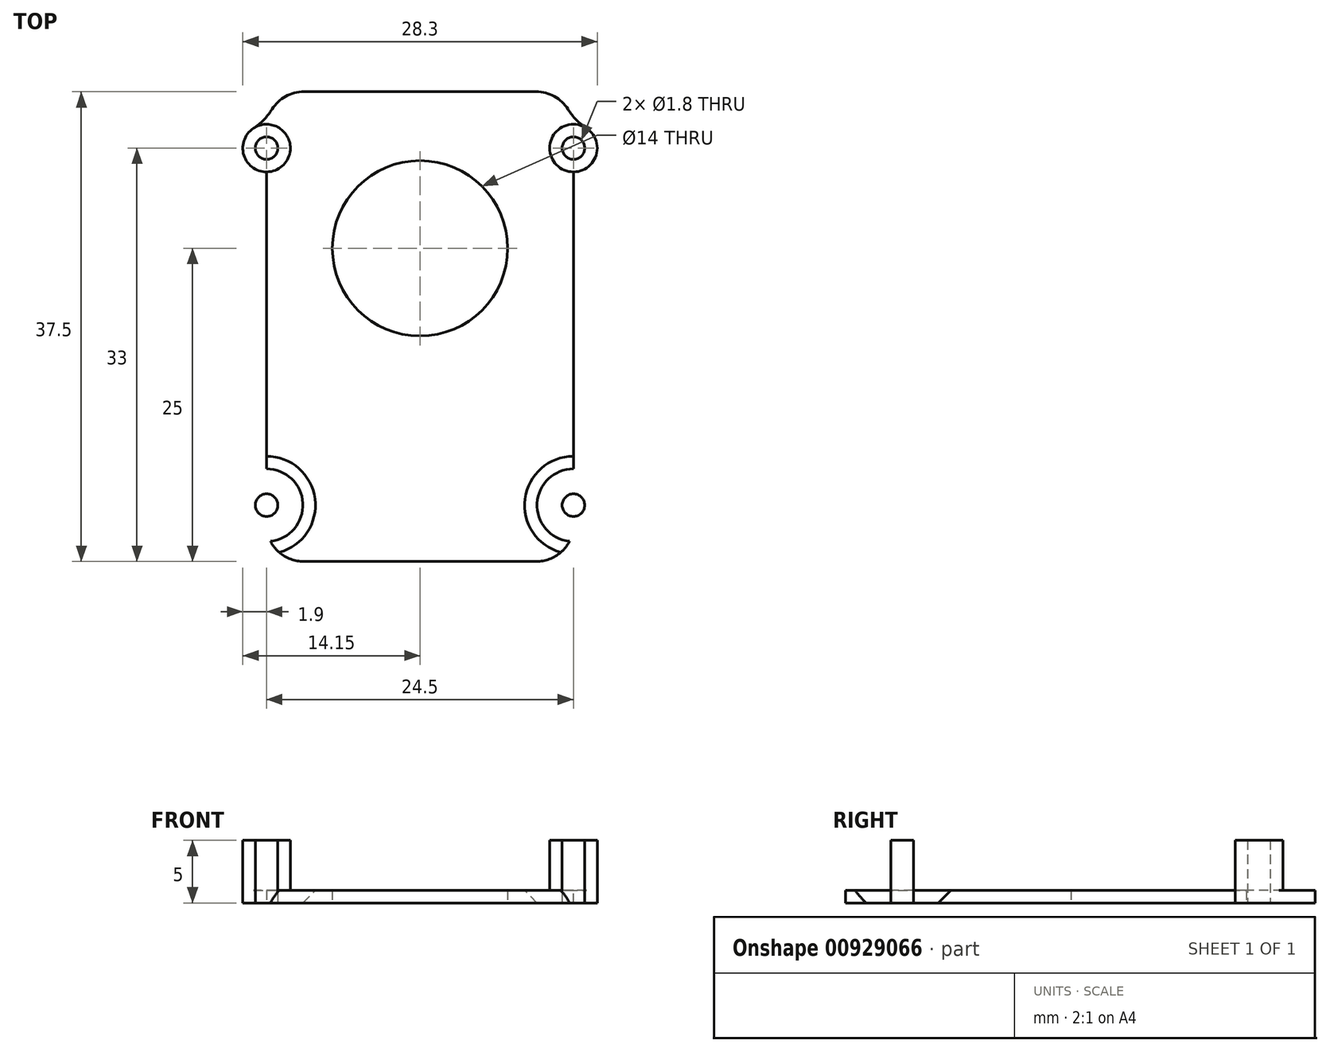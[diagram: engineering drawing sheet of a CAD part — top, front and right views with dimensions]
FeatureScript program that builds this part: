
annotation { "Feature Type Name" : "Feature", "Feature Type Description" : "" }
export const myFeature = defineFeature(function(context is Context, id is Id, definition is map)
    precondition{}
    {
        {
            var Q0;
            Q0=qCreatedBy(makeId("Top.planeOp"),FACE);
            var sketch = newSketch(context, id + "F0", { "sketchPlane" : qUnion([Q0])});
            skCircle(sketch, "E0", {"center": v(-12.25, 14.25) * mm, "radius": 0.9 * mm});
            skLineSegment(sketch, "E1", {"start": v(-12.25, 14.25) * mm, "end": v(12.25, 14.25) * mm, "construction": true});
            skCircle(sketch, "E2", {"center": v(12.25, 14.25) * mm, "radius": 0.9 * mm});
            skLineSegment(sketch, "E3", {"start": v(12.25, 0) * mm, "end": v(-12.25, 0) * mm, "construction": true});
            skLineSegment(sketch, "E4", {"start": v(0, 0) * mm, "end": v(0, 23) * mm, "construction": true});
            skCircle(sketch, "E5.0", {"center": v(-12.25, 14.25) * mm, "radius": 1.9 * mm});
            skCircle(sketch, "E6.0", {"center": v(12.25, 14.25) * mm, "radius": 1.9 * mm});
            skCircle(sketch, "E7.MirrorC", {"center": v(-12.25, -14.25) * mm, "radius": 1.9 * mm});
            skCircle(sketch, "E8.MirrorC", {"center": v(-12.25, -14.25) * mm, "radius": 0.9 * mm});
            skCircle(sketch, "E9.MirrorC", {"center": v(12.25, -14.25) * mm, "radius": 1.9 * mm});
            skCircle(sketch, "E10.MirrorC", {"center": v(12.25, -14.25) * mm, "radius": 0.9 * mm});
            skLineSegment(sketch, "E11", {"start": v(-12.25, -12.35) * mm, "end": v(-12.25, 12.35) * mm});
            skLineSegment(sketch, "E12", {"start": v(12.25, 12.35) * mm, "end": v(12.25, -12.35) * mm});
            skLineSegment(sketch, "E13", {"start": v(-12.25, 18.75) * mm, "end": v(12.25, 18.75) * mm});
            skLineSegment(sketch, "E14", {"start": v(-12.25, 18.75) * mm, "end": v(-12.25, 16.15) * mm});
            skLineSegment(sketch, "E15", {"start": v(12.25, 18.75) * mm, "end": v(12.25, 16.15) * mm});
            skLineSegment(sketch, "E16.MirrorCS", {"start": v(-12.25, -18.75) * mm, "end": v(-12.25, -16.15) * mm});
            skLineSegment(sketch, "E17.MirrorCS", {"start": v(-12.25, -18.75) * mm, "end": v(12.25, -18.75) * mm});
            skLineSegment(sketch, "E18.MirrorCS", {"start": v(12.25, -18.75) * mm, "end": v(12.25, -16.15) * mm});
            skCircle(sketch, "E19", {"center": v(0, 6.25) * mm, "radius": 7 * mm});
            skSolve(sketch);
        }
        {
            var Q0;
            {var subQ3=sQuery(id+"F0.wireOp",EDGE,"E11");Q0=makeQuery(id+"F0.imprint","IMPRINT",FACE,{"disambiguationData":[TD([[makeQuery(id+"F0.imprint","IMPRINT",EDGE,{"derivedFrom":subQ3}),-1.0]])]});}
            extrude(context, id + "F1", {"entities" : qUnion([Q0]), "depth" : 1 * mm, "offsetDistance" : 25 * mm});
        }
        {
            var Q0;
            Q0=makeQuery(id+"F0.imprint","IMPRINT",FACE,{"disambiguationData":[TD([[makeQuery(id+"F0.imprint","IMPRINT",EDGE,{"derivedFrom":sQuery(id+"F0.wireOp",EDGE,"E0")}),-1.0]])]});
            var Q1;
            Q1=makeQuery(id+"F0.imprint","IMPRINT",FACE,{"disambiguationData":[TD([[makeQuery(id+"F0.imprint","IMPRINT",EDGE,{"derivedFrom":sQuery(id+"F0.wireOp",EDGE,"E2")}),-1.0]])]});
            var Q2;
            Q2=makeQuery(id+"F0.imprint","IMPRINT",FACE,{"disambiguationData":[TD([[makeQuery(id+"F0.imprint","IMPRINT",EDGE,{"derivedFrom":sQuery(id+"F0.wireOp",EDGE,"E10.MirrorC")}),1.0]])]});
            var Q3;
            Q3=makeQuery(id+"F0.imprint","IMPRINT",FACE,{"disambiguationData":[TD([[makeQuery(id+"F0.imprint","IMPRINT",EDGE,{"derivedFrom":sQuery(id+"F0.wireOp",EDGE,"E8.MirrorC")}),1.0]])]});
            extrude(context, id + "F2", {"entities" : qUnion([Q0, Q1, Q2, Q3]), "operationType" : NewBodyOperationType.ADD, "depth" : 5 * mm, "offsetDistance" : 25 * mm});
        }
        {
            var Q0;
            Q0=makeQuery(id+"F1.opExtrude","SWEPT_EDGE",EDGE,{"disambiguationData":[OSD([sQuery(id+"F0.wireOp",EDGE,"E16.MirrorCS"),sQuery(id+"F0.wireOp",EDGE,"E17.MirrorCS")])]});
            var Q1;
            Q1=makeQuery(id+"F1.opExtrude","SWEPT_EDGE",EDGE,{"disambiguationData":[OSD([sQuery(id+"F0.wireOp",EDGE,"E17.MirrorCS"),sQuery(id+"F0.wireOp",EDGE,"E18.MirrorCS")])]});
            var Q2;
            Q2=makeQuery(id+"F1.opExtrude","SWEPT_EDGE",EDGE,{"disambiguationData":[OSD([sQuery(id+"F0.wireOp",EDGE,"E13"),sQuery(id+"F0.wireOp",EDGE,"E15")])]});
            var Q3;
            Q3=makeQuery(id+"F1.opExtrude","SWEPT_EDGE",EDGE,{"disambiguationData":[OSD([sQuery(id+"F0.wireOp",EDGE,"E13"),sQuery(id+"F0.wireOp",EDGE,"E14")])]});
            fillet(context, id + "F3", {"entities" : qUnion([Q0, Q1, Q2, Q3]), "radius" : 3 * mm, "tangentPropagation" : true, "allowEdgeOverflow" : false});
        }
        {
            var Q0;
            Q0=makeQuery(id+"F1.opExtrude","CAP_EDGE",EDGE,{"disambiguationData":[OSD([sQuery(id+"F0.wireOp",EDGE,"E5.0")])],"isStart":false});
            var Q1;
            Q1=makeQuery(id+"F1.opExtrude","CAP_EDGE",EDGE,{"disambiguationData":[OSD([sQuery(id+"F0.wireOp",EDGE,"E7.MirrorC")])],"isStart":false});
            var Q2;
            Q2=makeQuery(id+"F1.opExtrude","CAP_EDGE",EDGE,{"disambiguationData":[OSD([sQuery(id+"F0.wireOp",EDGE,"E9.MirrorC")])],"isStart":false});
            var Q3;
            Q3=makeQuery(id+"F1.opExtrude","CAP_EDGE",EDGE,{"disambiguationData":[OSD([sQuery(id+"F0.wireOp",EDGE,"E6.0")])],"isStart":false});
            chamfer(context, id + "F4", {"entities" : qUnion([Q0, Q1, Q2, Q3]), "width" : 2 * mm, "tangentPropagation" : true});
        }
        {
            var Q0;
            Q0=makeQuery(id+"F3.opFillet","BLEND_EDGE",EDGE,{"blendedFrom":[makeQuery(id+"F1.opExtrude","SWEPT_EDGE",EDGE,{"disambiguationData":[OSD([sQuery(id+"F0.wireOp",EDGE,"E17.MirrorCS"),sQuery(id+"F0.wireOp",EDGE,"E18.MirrorCS")])]}),makeQuery(id+"F2.opExtrude","SWEPT_FACE",FACE,{"disambiguationData":[OSD([sQuery(id+"F0.wireOp",EDGE,"E9.MirrorC")])]})],"blendedInto":[makeQuery(id+"F2.opExtrude","SWEPT_FACE",FACE,{"disambiguationData":[OSD([sQuery(id+"F0.wireOp",EDGE,"E9.MirrorC")])]})]});
            var Q1;
            Q1=makeQuery(id+"F1.opExtrude","SWEPT_EDGE",EDGE,{"disambiguationData":[OSD([sQuery(id+"F0.wireOp",EDGE,"E9.MirrorC"),sQuery(id+"F0.wireOp",EDGE,"E12")])]});
            var Q2;
            Q2=makeQuery(id+"F1.opExtrude","SWEPT_EDGE",EDGE,{"disambiguationData":[OSD([sQuery(id+"F0.wireOp",EDGE,"E7.MirrorC"),sQuery(id+"F0.wireOp",EDGE,"E11")])]});
            var Q3;
            Q3=makeQuery(id+"F3.opFillet","BLEND_EDGE",EDGE,{"blendedFrom":[makeQuery(id+"F1.opExtrude","SWEPT_EDGE",EDGE,{"disambiguationData":[OSD([sQuery(id+"F0.wireOp",EDGE,"E16.MirrorCS"),sQuery(id+"F0.wireOp",EDGE,"E17.MirrorCS")])]}),makeQuery(id+"F2.opExtrude","SWEPT_FACE",FACE,{"disambiguationData":[OSD([sQuery(id+"F0.wireOp",EDGE,"E7.MirrorC")])]})],"blendedInto":[makeQuery(id+"F2.opExtrude","SWEPT_FACE",FACE,{"disambiguationData":[OSD([sQuery(id+"F0.wireOp",EDGE,"E7.MirrorC")])]})]});
            var Q4;
            Q4=makeQuery(id+"F1.opExtrude","SWEPT_EDGE",EDGE,{"disambiguationData":[OSD([sQuery(id+"F0.wireOp",EDGE,"E5.0"),sQuery(id+"F0.wireOp",EDGE,"E11")])]});
            var Q5;
            Q5=makeQuery(id+"F3.opFillet","BLEND_EDGE",EDGE,{"blendedFrom":[makeQuery(id+"F1.opExtrude","SWEPT_EDGE",EDGE,{"disambiguationData":[OSD([sQuery(id+"F0.wireOp",EDGE,"E13"),sQuery(id+"F0.wireOp",EDGE,"E14")])]}),makeQuery(id+"F2.opExtrude","SWEPT_FACE",FACE,{"disambiguationData":[OSD([sQuery(id+"F0.wireOp",EDGE,"E5.0")])]})],"blendedInto":[makeQuery(id+"F2.opExtrude","SWEPT_FACE",FACE,{"disambiguationData":[OSD([sQuery(id+"F0.wireOp",EDGE,"E5.0")])]})]});
            var Q6;
            Q6=makeQuery(id+"F3.opFillet","BLEND_EDGE",EDGE,{"blendedFrom":[makeQuery(id+"F1.opExtrude","SWEPT_EDGE",EDGE,{"disambiguationData":[OSD([sQuery(id+"F0.wireOp",EDGE,"E13"),sQuery(id+"F0.wireOp",EDGE,"E15")])]}),makeQuery(id+"F2.opExtrude","SWEPT_FACE",FACE,{"disambiguationData":[OSD([sQuery(id+"F0.wireOp",EDGE,"E6.0")])]})],"blendedInto":[makeQuery(id+"F2.opExtrude","SWEPT_FACE",FACE,{"disambiguationData":[OSD([sQuery(id+"F0.wireOp",EDGE,"E6.0")])]})]});
            var Q7;
            Q7=makeQuery(id+"F1.opExtrude","SWEPT_EDGE",EDGE,{"disambiguationData":[OSD([sQuery(id+"F0.wireOp",EDGE,"E6.0"),sQuery(id+"F0.wireOp",EDGE,"E12")])]});
            fillet(context, id + "F5", {"entities" : qUnion([Q0, Q1, Q2, Q3, Q4, Q5, Q6, Q7]), "radius" : 5 * mm, "tangentPropagation" : true, "allowEdgeOverflow" : false});
        }
    });
